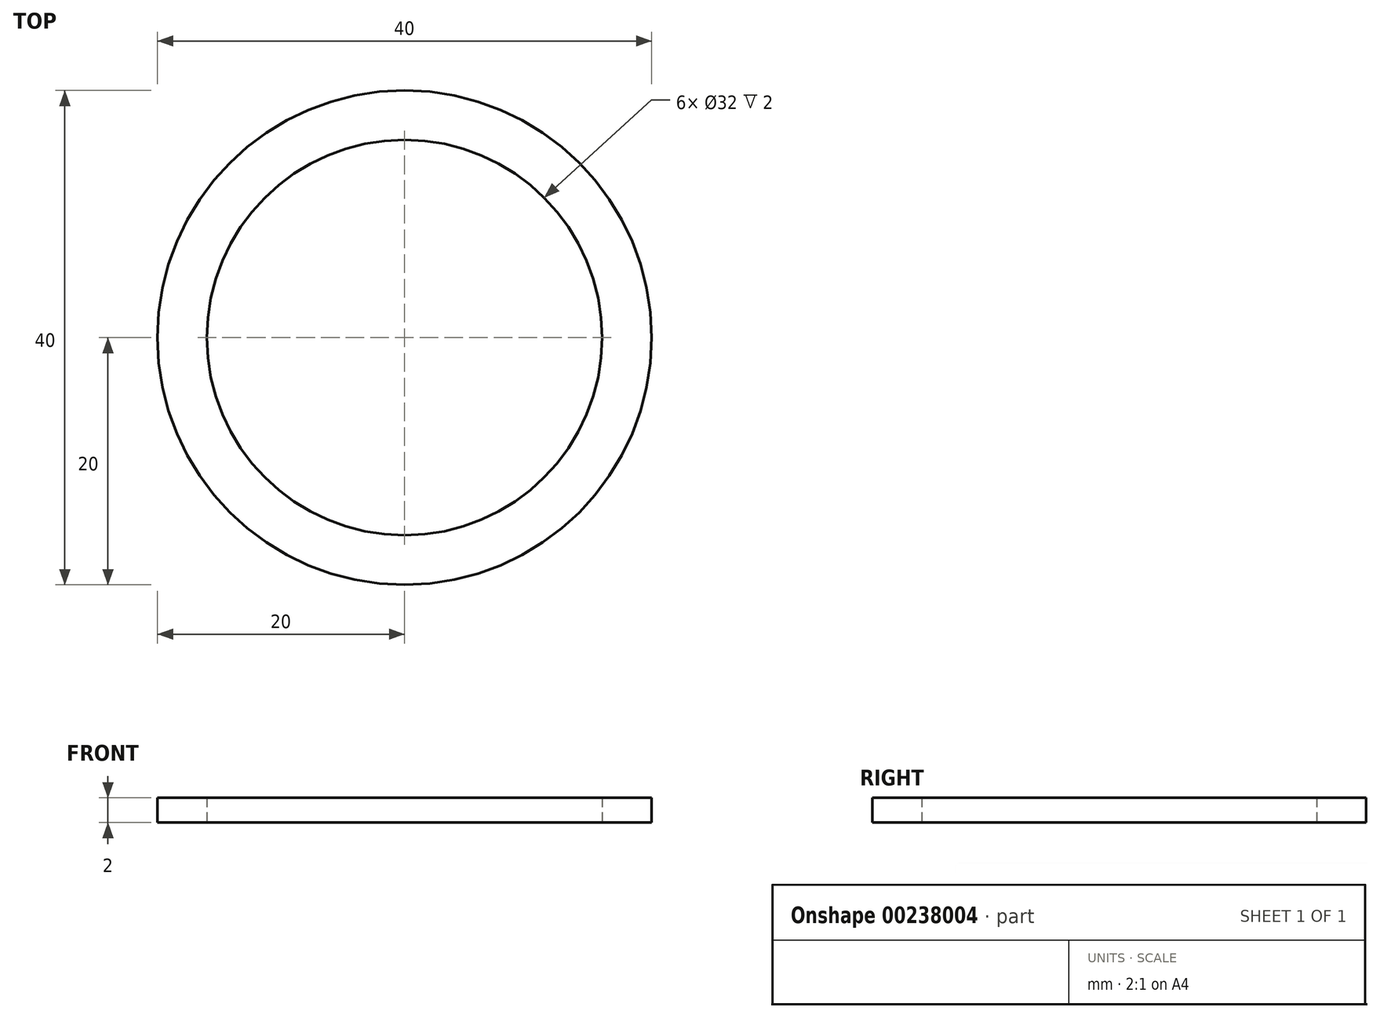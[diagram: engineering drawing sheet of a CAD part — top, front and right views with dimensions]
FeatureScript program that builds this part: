
annotation { "Feature Type Name" : "Feature", "Feature Type Description" : "" }
export const myFeature = defineFeature(function(context is Context, id is Id, definition is map)
    precondition{}
    {
        {
            var Q0;
            Q0=qCreatedBy(makeId("Top.planeOp"),FACE);
            var sketch = newSketch(context, id + "F0", { "sketchPlane" : qUnion([Q0])});
            skCircle(sketch, "E0", {"center": v(0, 0) * mm, "radius": 16 * mm});
            skCircle(sketch, "E1", {"center": v(0, 0) * mm, "radius": 20 * mm});
            skSolve(sketch);
        }
        {
            var Q0;
            Q0 = qSketchRegion(id + "F0", true);
            extrude(context, id + "F1", {"entities" : qUnion([Q0]), "depth" : 2 * mm});
        }
    });
